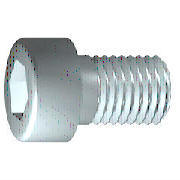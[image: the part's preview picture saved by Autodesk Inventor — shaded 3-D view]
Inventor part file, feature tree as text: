
AUTODESK INVENTOR PART (.ipt)
format: ipt  version: 2020 (Build 240168000, 168)  size: 196,096 bytes
history: native  units: mm (DEFAULTED — no unit token found)
features: sketch x2, other x1, extrude x1, plane x1, fillet x1
ambient origin geometry x7: Origin, YZ Plane, XY Plane, X Axis, Y Axis, Z Axis, Center Point
bodies: Solid1 (feature_tree)
feature tree (6):
  other  "Bryła"
  extrude  "Szczelina"  Depth=8.5mm
  plane  "Work Plane1"
  fillet  "Fillet2"  Radius=0.306825mm
  sketch  "Szkic1"
  sketch  "Szkic2"
